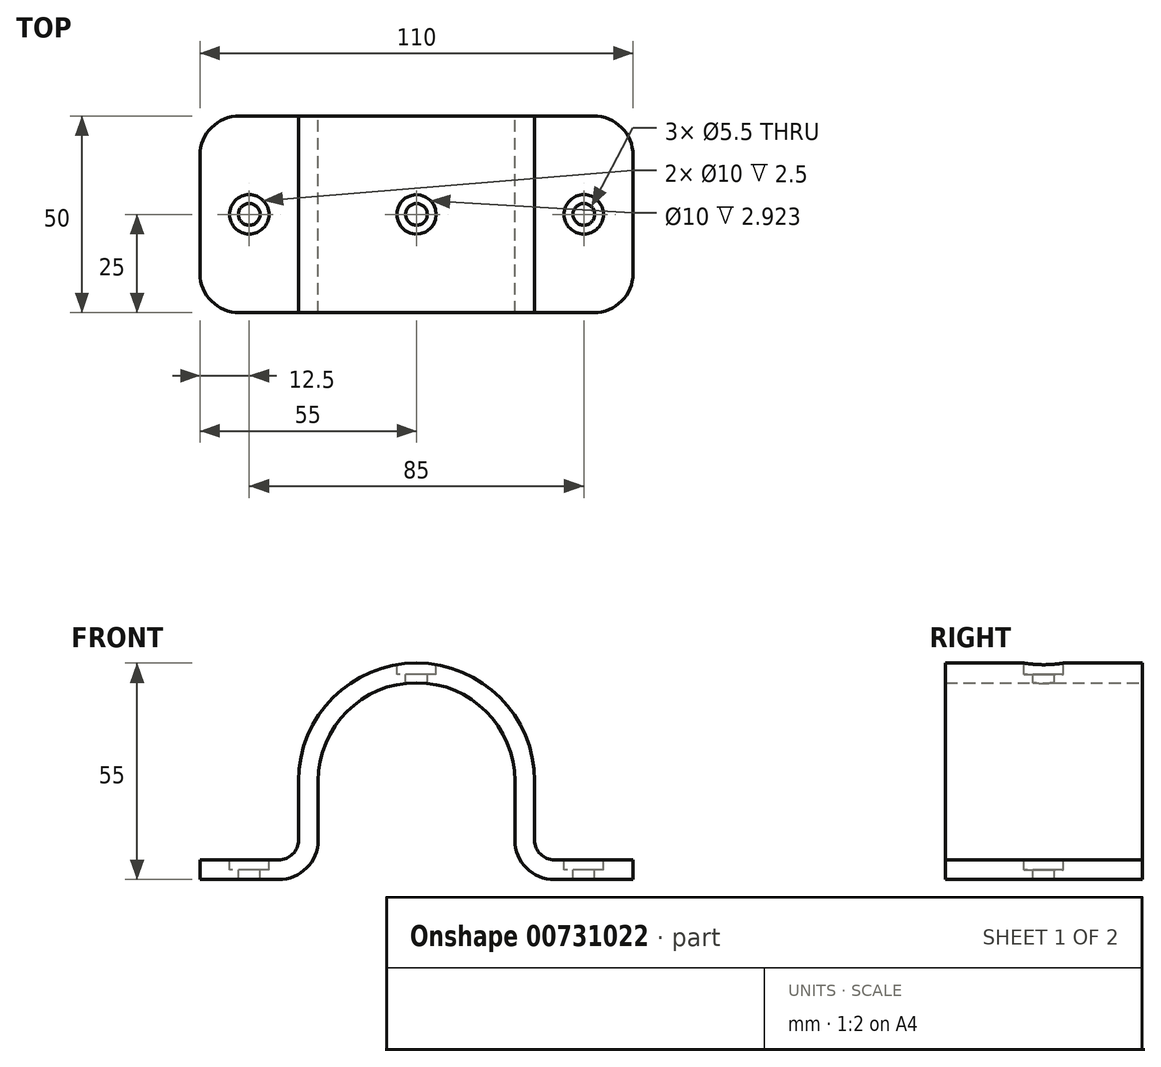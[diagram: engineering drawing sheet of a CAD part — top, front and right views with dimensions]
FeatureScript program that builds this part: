
annotation { "Feature Type Name" : "Feature", "Feature Type Description" : "" }
export const myFeature = defineFeature(function(context is Context, id is Id, definition is map)
    precondition{}
    {
        {
            var Q0;
            Q0=qCreatedBy(makeId("Front.planeOp"),FACE);
            var sketch = newSketch(context, id + "F0", { "sketchPlane" : qUnion([Q0])});
            skLineSegment(sketch, "E0", {"start": v(-55, -25) * mm, "end": v(-25, -25) * mm});
            skLineSegment(sketch, "E1", {"start": v(-25, -25) * mm, "end": v(-25, 0) * mm});
            skArc(sketch, "E2", {"start": v(25, 0) * mm, "mid": v(0, 25) * mm, "end": v(-25, 0) * mm});
            skLineSegment(sketch, "E3", {"start": v(25, 0) * mm, "end": v(25, -25) * mm});
            skLineSegment(sketch, "E4", {"start": v(25, -25) * mm, "end": v(55, -25) * mm});
            skArc(sketch, "E5.1", {"start": v(30, 0) * mm, "mid": v(0, 30) * mm, "end": v(-30, 0) * mm});
            skLineSegment(sketch, "E6", {"start": v(-55, -25) * mm, "end": v(-55, -20) * mm});
            skLineSegment(sketch, "E7", {"start": v(55, -25) * mm, "end": v(55, -20) * mm});
            skLineSegment(sketch, "E8", {"start": v(30, 0) * mm, "end": v(30, -20) * mm});
            skLineSegment(sketch, "E9", {"start": v(30, -20) * mm, "end": v(55, -20) * mm});
            skLineSegment(sketch, "E10", {"start": v(-30, 0) * mm, "end": v(-30, -20) * mm});
            skLineSegment(sketch, "E11", {"start": v(-30, -20) * mm, "end": v(-55, -20) * mm});
            skSolve(sketch);
        }
        {
            var Q0;
            Q0=makeQuery(id+"F0.imprint","IMPRINT",FACE,{"disambiguationData":[TD([[makeQuery(id+"F0.imprint","IMPRINT",EDGE,{"derivedFrom":sQuery(id+"F0.wireOp",EDGE,"E0")}),1.0]])]});
            extrude(context, id + "F1", {"entities" : qUnion([Q0]), "endBound" : BoundingType.SYMMETRIC, "depth" : 50 * mm, "offsetDistance" : 25 * mm});
        }
        {
            var Q0;
            Q0=makeQuery(id+"F1.opExtrude","CAP_EDGE",EDGE,{"disambiguationData":[OSD([sQuery(id+"F0.wireOp",EDGE,"E5.1")])],"isStart":true});
            cPoint(context, id + "F2", {"entities" : qUnion([Q0]), "parameter" : 0.5});
        }
        {
            var Q0;
            Q0=qCreatedBy(makeId("Top.planeOp"),FACE);
            var Q1;
            Q1 = qCreatedBy(id + "F2" ,VERTEX);
            cPlane(context, id + "F3", {"entities" : qUnion([Q0, Q1]), "cplaneType" : CPlaneType.PLANE_POINT, "offset" : 25 * mm, "width" : 150 * mm, "height" : 150 * mm});
        }
        {
            var Q0;
            Q0=qCreatedBy(id+"F3.planeOp",FACE);
            var sketch = newSketch(context, id + "F4", { "sketchPlane" : qUnion([Q0])});
            skPoint(sketch, "E12", {"position": v(0, 0) * mm});
            skSolve(sketch);
        }
        {
            var Q0;
            Q0=sQuery(id+"F4.wireOp",VERTEX,"E12");
            var Q1;
            Q1=makeQuery(id+"F1.opExtrude","SWEPT_BODY",BODY,{"disambiguationData":[OSD([sQuery(id+"F0.wireOp",EDGE,"E0"),sQuery(id+"F0.wireOp",EDGE,"E1"),sQuery(id+"F0.wireOp",EDGE,"E2"),sQuery(id+"F0.wireOp",EDGE,"E3"),sQuery(id+"F0.wireOp",EDGE,"E4"),sQuery(id+"F0.wireOp",EDGE,"E5.0"),sQuery(id+"F0.wireOp",EDGE,"E5.1"),sQuery(id+"F0.wireOp",EDGE,"E5.2"),sQuery(id+"F0.wireOp",EDGE,"E6"),sQuery(id+"F0.wireOp",EDGE,"E7")])]});
            hole(context, id + "F5", {"style" : HoleStyle.C_BORE, "endStyle" : HoleEndStyle.THROUGH, "holeDiameter" : 5.5 * mm, "cBoreDiameter" : 10 * mm, "cBoreDepth" : 2.5 * mm, "majorDiameter" : 10 * mm, "isTappedThrough" : true, "tappedDepth" : 12 * mm, "tapClearance" : 3, "locations" : qUnion([Q0]), "scope" : qUnion([Q1])});
        }
        {
            var Q0;
            Q0=makeQuery(id+"F1.opExtrude","SWEPT_FACE",FACE,{"disambiguationData":[OSD([sQuery(id+"F0.wireOp",EDGE,"E11")])]});
            var sketch = newSketch(context, id + "F6", { "sketchPlane" : qUnion([Q0])});
            skPoint(sketch, "E13", {"position": v(-42.5, 0) * mm});
            skPoint(sketch, "E14", {"position": v(42.5, 0) * mm});
            skSolve(sketch);
        }
        {
            var Q0;
            Q0=sQuery(id+"F6.wireOp",VERTEX,"E13");
            var Q1;
            Q1=sQuery(id+"F6.wireOp",VERTEX,"E14");
            var Q2;
            Q2=makeQuery(id+"F1.opExtrude","SWEPT_BODY",BODY,{"disambiguationData":[OSD([sQuery(id+"F0.wireOp",EDGE,"E0"),sQuery(id+"F0.wireOp",EDGE,"E1"),sQuery(id+"F0.wireOp",EDGE,"E2"),sQuery(id+"F0.wireOp",EDGE,"E3"),sQuery(id+"F0.wireOp",EDGE,"E4"),sQuery(id+"F0.wireOp",EDGE,"E5.1"),sQuery(id+"F0.wireOp",EDGE,"E6"),sQuery(id+"F0.wireOp",EDGE,"E7"),sQuery(id+"F0.wireOp",EDGE,"E8"),sQuery(id+"F0.wireOp",EDGE,"E9"),sQuery(id+"F0.wireOp",EDGE,"E10"),sQuery(id+"F0.wireOp",EDGE,"E11")])]});
            hole(context, id + "F7", {"style" : HoleStyle.C_BORE, "endStyle" : HoleEndStyle.THROUGH, "holeDiameter" : 5.5 * mm, "cBoreDiameter" : 10 * mm, "cBoreDepth" : 2.5 * mm, "majorDiameter" : 5 * mm, "isTappedThrough" : true, "tappedDepth" : 12 * mm, "tapClearance" : 3, "locations" : qUnion([Q0, Q1]), "scope" : qUnion([Q2])});
        }
        {
            var Q0;
            Q0=makeQuery(id+"F1.opExtrude","SWEPT_EDGE",EDGE,{"disambiguationData":[OSD([sQuery(id+"F0.wireOp",EDGE,"E8"),sQuery(id+"F0.wireOp",EDGE,"E9")])]});
            var Q1;
            Q1=makeQuery(id+"F1.opExtrude","SWEPT_EDGE",EDGE,{"disambiguationData":[OSD([sQuery(id+"F0.wireOp",EDGE,"E10"),sQuery(id+"F0.wireOp",EDGE,"E11")])]});
            fillet(context, id + "F8", {"entities" : qUnion([Q0, Q1]), "radius" : 5 * mm, "tangentPropagation" : true, "allowEdgeOverflow" : false});
        }
        {
            var Q0;
            Q0=makeQuery(id+"F1.opExtrude","SWEPT_EDGE",EDGE,{"disambiguationData":[OSD([sQuery(id+"F0.wireOp",EDGE,"E3"),sQuery(id+"F0.wireOp",EDGE,"E4")])]});
            var Q1;
            Q1=makeQuery(id+"F1.opExtrude","SWEPT_EDGE",EDGE,{"disambiguationData":[OSD([sQuery(id+"F0.wireOp",EDGE,"E0"),sQuery(id+"F0.wireOp",EDGE,"E1")])]});
            fillet(context, id + "F9", {"entities" : qUnion([Q0, Q1]), "radius" : 10 * mm, "tangentPropagation" : true, "allowEdgeOverflow" : false});
        }
        {
            var Q0;
            Q0=makeQuery(id+"F1.opExtrude","CAP_EDGE",EDGE,{"disambiguationData":[OSD([sQuery(id+"F0.wireOp",EDGE,"E6")])],"isStart":false});
            var Q1;
            Q1=makeQuery(id+"F1.opExtrude","CAP_EDGE",EDGE,{"disambiguationData":[OSD([sQuery(id+"F0.wireOp",EDGE,"E7")])],"isStart":false});
            var Q2;
            Q2=makeQuery(id+"F1.opExtrude","CAP_EDGE",EDGE,{"disambiguationData":[OSD([sQuery(id+"F0.wireOp",EDGE,"E7")])],"isStart":true});
            var Q3;
            Q3=makeQuery(id+"F1.opExtrude","CAP_EDGE",EDGE,{"disambiguationData":[OSD([sQuery(id+"F0.wireOp",EDGE,"E6")])],"isStart":true});
            fillet(context, id + "F10", {"entities" : qUnion([Q0, Q1, Q2, Q3]), "radius" : 10 * mm, "tangentPropagation" : true, "allowEdgeOverflow" : false});
        }
    });
